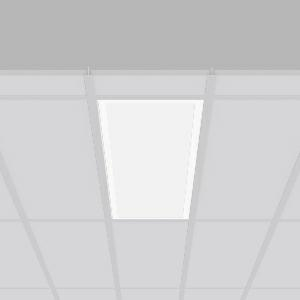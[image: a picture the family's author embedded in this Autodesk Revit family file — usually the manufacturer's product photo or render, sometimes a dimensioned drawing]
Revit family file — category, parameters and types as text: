
# Revit family: sidelite_eco_672377_002_07_bc15
name_source: partatom
category: Lighting Fixtures
units: mm (PartAtom-declared; Revit-internal decimal feet)

## family parameters
Cut with Voids When Loaded = No
Host = Face
Light Source = No
Part Type = Normal
Room Calculation Point = No
Round Connector Dimension = Use Diameter
Shared = No

## types (1)
- SIDELITE ECO (1 x LED Modul 830, 3300 lm, 3000)
    Apparent Load = 29 VA
    CIE Flux Codes = 47 79 96 100 100
    Color Rendering = 80
    Color Temperature = 3000
    Default Elevation = 1800 mm
    Description = Series: SIDELITE ECO
Highly economical recessed luminaire with progressive LED technology. For escape route illumination. Frame made of aluminium, powder-coated. Diffuser: plastic, opal. Lightguide and diffuser made of non-yellowing plastic (PMMA). Lateral light emission (RZB SIDELITE technology) for homogeneous light distribution. External driver. Self-contained system with automatic self-test and feedback via DALI bus, only to RZB DALI monitoring system. External driver with simple plug-in locking system. Extended connection cable (1.90 m). 
Colour: white
Length: 1245 mm
Width: 308 mm
Cut-out length: 1220 mm
Cut-out width: 285 mm
Recess height: 160 mm
Luminaire: recess height: 40 mm
Weight: 4.7 kg
Operating mode: maintained power mode
Duration time: 3 h
Lamp: LED
Socket: without socket
Colour temperature: 3000K
Colour rendering index (CRI): 80
System power: 29 W
Rated luminous flux: 3300 lm
Luminous flux, emergency: 480 lm
System power, emergency: -
Control gear: Regulated power supply
Protection class: I
Type of protection: IP 40
    Height = 0 mm  [stored 0 ft]
    Lamp = 1 x LED Modul 830
    Lamp Light Flux = 3300 lm
    Lamp count = 1
    Length = 1245 mm
    Lifetime = 50000 h
    Luminous efficacy = 114 lm/W
    Manufacturer = RZB
    ModVariant = No
    Model = 672377.002.07
    Mounting Place = Ceiling
    Mounting Type = Recessed
    Number of Poles = 1
    OnlyDefault = Yes
    Power Factor = 1
    Product Name = SIDELITE ECO
    Product group = Recessed modular luminaires
    ProductGroupID = 406
    Protection Class = Protection class I
    Protection Degree = IP 40
    RLX_Detail_Level = 1
    RLX_Emergency_Light_Flux = 480 lm
    RLX_Emergency_Type = 3
    RLX_Emergency_Type_DB = Yes
    RlxData = <blob elided: 30237 chars, md5=21e09875>
    Socket = socket
    Standby Power = 0 W
    System Light Flux = 3300 lm
    System Power = 29 W
    Type Comments = Product without accessories
    Type Image = 312367.002.jpg
    URL = http://relux.com
    VarID = ---
    Voltage = 230 V
    Voltage Range = 220-240 V
    Weight = 0.00 kg
    Width = 308 mm

note: [stored X ft] marks values corroborated as IEEE doubles in the binary element streams (Revit-internal decimal feet)

## geometry (parser evidence)
native form markers: Blend x4, Sweep x12
no freeform markers — native parametric forms only
